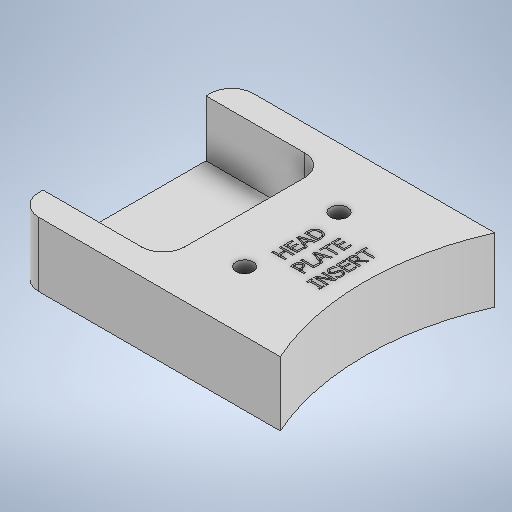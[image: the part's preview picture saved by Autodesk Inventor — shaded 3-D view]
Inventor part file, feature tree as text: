
AUTODESK INVENTOR PART (.ipt)
format: ipt  version: 2025 (Build 290162000, 162)  size: 477,184 bytes
history: native  units: mm
features: sketch x5, extrude x3, hole x1, fillet x1, emboss x1
ambient origin geometry x8: Origin, YZ Plane, XZ Plane, XY Plane, X Axis, Y Axis, Z Axis, Center Point
bodies: Solid1 (feature_tree)
feature tree (11):
  extrude  "Head Plate Geometry"  Depth=5.0mm
  extrude  "Magnet Seat"  Depth=28.0mm
  hole  "Hole1"  [1 undecoded]
  fillet  "Fillet1"  Radius=11.0mm
  extrude  "Remove Material"  Depth=1.0mm
  emboss  "Emboss1"
  sketch  "Sketch1"  dims[d0=85.0mm d1=61.0mm d2=235.0mm d4=15.0mm d5=0.0mm d6=5.0mm]
  sketch  "Sketch2"  dims[d7=38.0mm d8=28.0mm]
  sketch  "Sketch3"  dims[d9=13.1mm d10=0.0mm]
  sketch  "Sketch4"  dims[d11=4.0mm d12=6.0mm d13=8.0mm d14=6.0mm d15=90.0deg d16=3.0mm d17=0.0mm d19=39.0mm d22=11.0mm]
  sketch  "Sketch5"  dims[d23=5.0mm d24=123.0mm d25=0.0mm d26=0.0mm d27=1.0mm d28=0.0mm]
note: 1 required parameter value undecoded (feature->parameter linkage not recoverable at this tier; creation-order binding heuristic only, values carry confidence <= 0.55)
